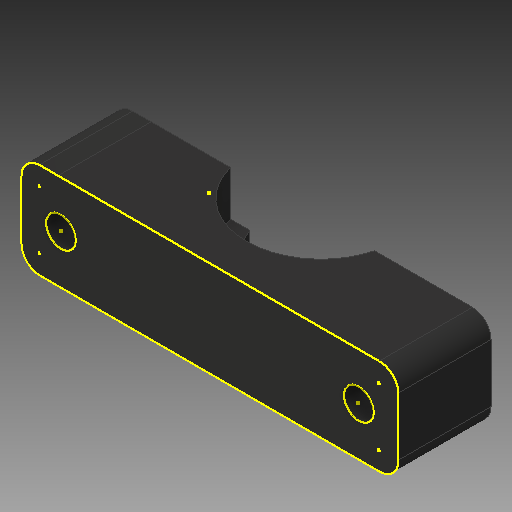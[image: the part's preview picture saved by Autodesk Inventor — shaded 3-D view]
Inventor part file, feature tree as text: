
AUTODESK INVENTOR PART (.ipt)
format: ipt  version: 2017 (Build 210142000, 142)  size: 138,240 bytes
history: native  units: mm
features: sketch x5, other x3
ambient origin geometry x8: Origin, YZ Plane, XZ Plane, XY Plane, X Axis, Y Axis, Z Axis, Center Point
bodies: Solid1 (feature_tree)
feature tree (8):
  other  "Hotend Clamp P1.ipt"
  other  "Solid1::Hotend Clamp P1.ipt"
  other  "TaggingFeature1"
  sketch  "Sketch1"  dims[d0=10.0mm]
  sketch  "Sketch2"
  sketch  "Sketch3"
  sketch  "Sketch4"
  sketch  "Sketch5"
